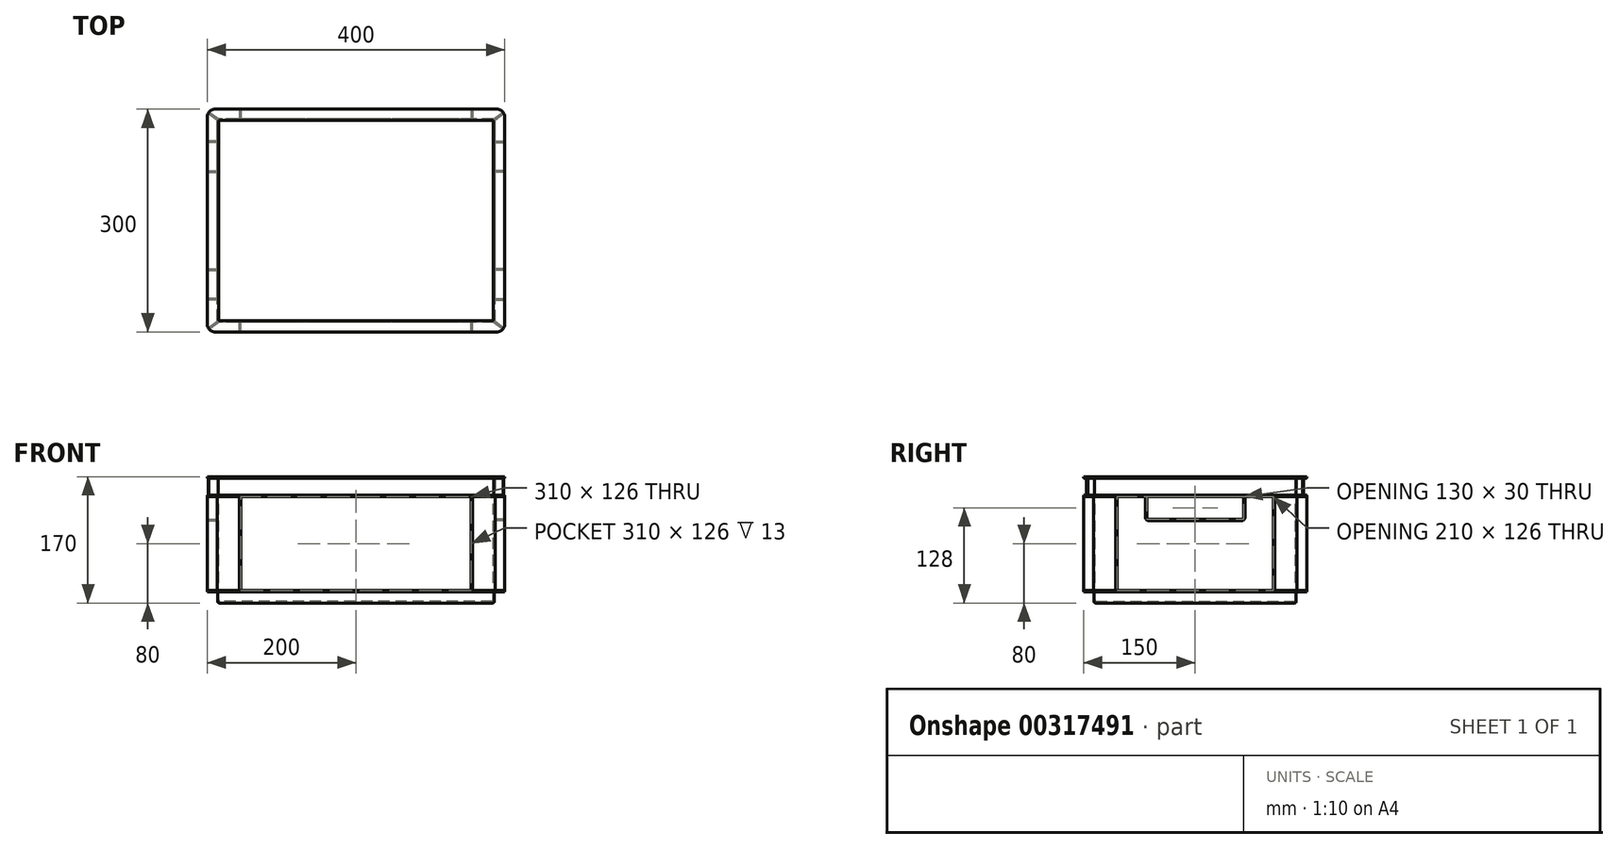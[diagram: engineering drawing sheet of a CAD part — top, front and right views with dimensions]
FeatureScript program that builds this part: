
annotation { "Feature Type Name" : "Feature", "Feature Type Description" : "" }
export const myFeature = defineFeature(function(context is Context, id is Id, definition is map)
    precondition{}
    {
        {
            var Q0;
            Q0=qCreatedBy(makeId("Top.planeOp"),FACE);
            var sketch = newSketch(context, id + "F0", { "sketchPlane" : qUnion([Q0])});
            skLineSegment(sketch, "E0.bottom", {"start": v(186, -136) * mm, "end": v(-186, -136) * mm});
            skLineSegment(sketch, "E0.top", {"start": v(186, 136) * mm, "end": v(-186, 136) * mm});
            skLineSegment(sketch, "E0.left", {"start": v(186, -136) * mm, "end": v(186, 136) * mm});
            skLineSegment(sketch, "E0.right", {"start": v(-186, -136) * mm, "end": v(-186, 136) * mm});
            skPoint(sketch, "E0.middle", {"position": v(0, 0) * mm});
            skPoint(sketch, "E1.visualSharp", {"position": v(-186, 136) * mm});
            skPoint(sketch, "E2.visualSharp", {"position": v(186, 136) * mm});
            skPoint(sketch, "E3.visualSharp", {"position": v(186, -136) * mm});
            skPoint(sketch, "E4.visualSharp", {"position": v(-186, -136) * mm});
            skSolve(sketch);
        }
        {
            var Q0;
            Q0=qSketchRegion(id+"F0",true);
            extrude(context, id + "F1", {"entities" : qUnion([Q0]), "depth" : 15 * mm});
        }
        {
            var Q0;
            Q0=makeQuery(id+"F1.opExtrude","CAP_FACE",FACE,{"disambiguationData":[OSD([sQuery(id+"F0.wireOp",EDGE,"E0.bottom"),sQuery(id+"F0.wireOp",EDGE,"E0.top"),sQuery(id+"F0.wireOp",EDGE,"E0.left"),sQuery(id+"F0.wireOp",EDGE,"E0.right")])],"isStart":false});
            var sketch = newSketch(context, id + "F2", { "sketchPlane" : qUnion([Q0])});
            skLineSegment(sketch, "E5.bottom", {"start": v(190, -150) * mm, "end": v(-190, -150) * mm});
            skLineSegment(sketch, "E5.top", {"start": v(190, 150) * mm, "end": v(-190, 150) * mm});
            skLineSegment(sketch, "E5.left", {"start": v(200, -140) * mm, "end": v(200, 140) * mm});
            skLineSegment(sketch, "E5.right", {"start": v(-200, -140) * mm, "end": v(-200, 140) * mm});
            skPoint(sketch, "E5.middle", {"position": v(0, 0) * mm});
            skPoint(sketch, "E6.visualSharp", {"position": v(-200, 150) * mm});
            skArc(sketch, "E6.filletArc", {"start": v(-190, 150) * mm, "mid": v(-197.07, 147.07) * mm, "end": v(-200, 140) * mm});
            skPoint(sketch, "E7.visualSharp", {"position": v(200, 150) * mm});
            skArc(sketch, "E7.filletArc", {"start": v(200, 140) * mm, "mid": v(197.07, 147.07) * mm, "end": v(190, 150) * mm});
            skPoint(sketch, "E8.visualSharp", {"position": v(200, -150) * mm});
            skArc(sketch, "E8.filletArc", {"start": v(190, -150) * mm, "mid": v(197.07, -147.07) * mm, "end": v(200, -140) * mm});
            skPoint(sketch, "E9.visualSharp", {"position": v(-200, -150) * mm});
            skArc(sketch, "E9.filletArc", {"start": v(-200, -140) * mm, "mid": v(-197.07, -147.07) * mm, "end": v(-190, -150) * mm});
            skSolve(sketch);
        }
        {
            var Q0;
            Q0=makeQuery(id+"F2.imprint","IMPRINT",FACE,{"disambiguationData":[TD([[makeQuery(id+"F2.imprint","IMPRINT",EDGE,{"derivedFrom":makeQuery(id+"F1.opExtrude","CAP_EDGE",EDGE,{"disambiguationData":[OSD([sQuery(id+"F0.wireOp",EDGE,"E0.bottom")])],"isStart":false})}),-1.0]])]});
            var Q1;
            Q1=makeQuery(id+"F2.imprint","IMPRINT",FACE,{"disambiguationData":[TD([[makeQuery(id+"F2.imprint","IMPRINT",EDGE,{"derivedFrom":sQuery(id+"F2.wireOp",EDGE,"E5.bottom")}),-1.0]])]});
            extrude(context, id + "F3", {"entities" : qUnion([Q0, Q1]), "operationType" : NewBodyOperationType.ADD, "depth" : 2 * mm});
        }
        {
            var Q0;
            Q0=makeQuery(id+"F3.opExtrude","CAP_FACE",FACE,{"disambiguationData":[OSD([sQuery(id+"F2.wireOp",EDGE,"E5.bottom"),sQuery(id+"F2.wireOp",EDGE,"E5.top"),sQuery(id+"F2.wireOp",EDGE,"E5.left"),sQuery(id+"F2.wireOp",EDGE,"E5.right"),sQuery(id+"F2.wireOp",EDGE,"E6.filletArc"),sQuery(id+"F2.wireOp",EDGE,"E7.filletArc"),sQuery(id+"F2.wireOp",EDGE,"E8.filletArc"),sQuery(id+"F2.wireOp",EDGE,"E9.filletArc")])],"isStart":false});
            var sketch = newSketch(context, id + "F4", { "sketchPlane" : qUnion([Q0])});
            skLineSegment(sketch, "E10.bottom", {"start": v(187, -137) * mm, "end": v(157, -137) * mm});
            skLineSegment(sketch, "E10.top", {"start": v(187, 137) * mm, "end": v(157, 137) * mm});
            skLineSegment(sketch, "E10.left", {"start": v(187, -137) * mm, "end": v(187, -107) * mm});
            skLineSegment(sketch, "E10.right", {"start": v(-187, -137) * mm, "end": v(-187, -107) * mm});
            skPoint(sketch, "E10.middle", {"position": v(0, 0) * mm});
            skLineSegment(sketch, "E11.bottom", {"start": v(-155, -150) * mm, "end": v(-157, -150) * mm});
            skLineSegment(sketch, "E11.left", {"start": v(-155, -150) * mm, "end": v(-155, -137) * mm});
            skLineSegment(sketch, "E11.right", {"start": v(-157, -150) * mm, "end": v(-157, -137) * mm});
            skPoint(sketch, "E11.middle", {"position": v(-156, -143.5) * mm});
            skLineSegment(sketch, "E12.trimOffspring", {"start": v(-157, -137) * mm, "end": v(-187, -137) * mm});
            skLineSegment(sketch, "E13.bottom", {"start": v(-187, -107) * mm, "end": v(-200, -107) * mm});
            skLineSegment(sketch, "E13.top", {"start": v(-187, -105) * mm, "end": v(-200, -105) * mm});
            skLineSegment(sketch, "E13.right", {"start": v(-200, -107) * mm, "end": v(-200, -105) * mm});
            skPoint(sketch, "E13.middle", {"position": v(-193.5, -106) * mm});
            skLineSegment(sketch, "E14.trimOffspring", {"start": v(-187, -105) * mm, "end": v(-187, 105) * mm});
            skLineSegment(sketch, "E15.MirrorCS", {"start": v(200, -107) * mm, "end": v(200, -105) * mm});
            skLineSegment(sketch, "E16.MirrorCS", {"start": v(155, -150) * mm, "end": v(155, -137) * mm});
            skLineSegment(sketch, "E17.MirrorCS", {"start": v(155, -150) * mm, "end": v(157, -150) * mm});
            skLineSegment(sketch, "E18.MirrorCS", {"start": v(157, -150) * mm, "end": v(157, -137) * mm});
            skLineSegment(sketch, "E19.MirrorCS", {"start": v(187, -105) * mm, "end": v(200, -105) * mm});
            skLineSegment(sketch, "E20.MirrorCS", {"start": v(187, -107) * mm, "end": v(200, -107) * mm});
            skPoint(sketch, "E21.MirrorP", {"position": v(193.5, -106) * mm});
            skLineSegment(sketch, "E22.trimOffspring", {"start": v(187, -105) * mm, "end": v(187, 105) * mm});
            skLineSegment(sketch, "E23.trimOffspring", {"start": v(155, -137) * mm, "end": v(-155, -137) * mm});
            skLineSegment(sketch, "E24.MirrorCS", {"start": v(-200, 107) * mm, "end": v(-200, 105) * mm});
            skPoint(sketch, "E25.MirrorP", {"position": v(-193.5, 106) * mm});
            skLineSegment(sketch, "E26.MirrorCS", {"start": v(-187, 105) * mm, "end": v(-200, 105) * mm});
            skLineSegment(sketch, "E27.MirrorCS", {"start": v(-187, 107) * mm, "end": v(-200, 107) * mm});
            skLineSegment(sketch, "E28.MirrorCS", {"start": v(-155, 150) * mm, "end": v(-157, 150) * mm});
            skLineSegment(sketch, "E29.MirrorCS", {"start": v(-157, 150) * mm, "end": v(-157, 137) * mm});
            skPoint(sketch, "E30.MirrorP", {"position": v(-156, 143.5) * mm});
            skLineSegment(sketch, "E31.MirrorCS", {"start": v(-155, 150) * mm, "end": v(-155, 137) * mm});
            skLineSegment(sketch, "E32.MirrorCS", {"start": v(155, 150) * mm, "end": v(157, 150) * mm});
            skLineSegment(sketch, "E33.MirrorCS", {"start": v(155, 150) * mm, "end": v(155, 137) * mm});
            skLineSegment(sketch, "E34.MirrorCS", {"start": v(157, 150) * mm, "end": v(157, 137) * mm});
            skLineSegment(sketch, "E35.MirrorCS", {"start": v(200, 107) * mm, "end": v(200, 105) * mm});
            skLineSegment(sketch, "E36.MirrorCS", {"start": v(187, 105) * mm, "end": v(200, 105) * mm});
            skPoint(sketch, "E37.MirrorP", {"position": v(193.5, 106) * mm});
            skLineSegment(sketch, "E38.MirrorCS", {"start": v(187, 107) * mm, "end": v(200, 107) * mm});
            skLineSegment(sketch, "E39.trimOffspring", {"start": v(-187, 107) * mm, "end": v(-187, 137) * mm});
            skLineSegment(sketch, "E40.trimOffspring", {"start": v(-157, 137) * mm, "end": v(-187, 137) * mm});
            skLineSegment(sketch, "E41.trimOffspring", {"start": v(155, 137) * mm, "end": v(-155, 137) * mm});
            skLineSegment(sketch, "E42.trimOffspring", {"start": v(187, 107) * mm, "end": v(187, 137) * mm});
            skSolve(sketch);
        }
        {
            var Q0;
            Q0=qSketchRegion(id+"F4",true);
            extrude(context, id + "F5", {"entities" : qUnion([Q0]), "operationType" : NewBodyOperationType.ADD, "depth" : 126 * mm});
        }
        {
            var Q0;
            Q0=makeQuery(id+"F5.opExtrude","CAP_FACE",FACE,{"disambiguationData":[OSD([sQuery(id+"F4.wireOp",EDGE,"E10.bottom"),sQuery(id+"F4.wireOp",EDGE,"E10.top"),sQuery(id+"F4.wireOp",EDGE,"E10.left"),sQuery(id+"F4.wireOp",EDGE,"E10.right")])],"isStart":false});
            var sketch = newSketch(context, id + "F6", { "sketchPlane" : qUnion([Q0])});
            skArc(sketch, "E43.0", {"start": v(-190, 150) * mm, "mid": v(-197.07, 147.07) * mm, "end": v(-200, 140) * mm});
            skArc(sketch, "E43.1", {"start": v(-200, -140) * mm, "mid": v(-197.07, -147.07) * mm, "end": v(-190, -150) * mm});
            skArc(sketch, "E43.2", {"start": v(190, -150) * mm, "mid": v(197.07, -147.07) * mm, "end": v(200, -140) * mm});
            skArc(sketch, "E43.3", {"start": v(200, 140) * mm, "mid": v(197.07, 147.07) * mm, "end": v(190, 150) * mm});
            skLineSegment(sketch, "E44", {"start": v(-200, 140) * mm, "end": v(-200, -140) * mm});
            skLineSegment(sketch, "E45", {"start": v(-190, -150) * mm, "end": v(190, -150) * mm});
            skLineSegment(sketch, "E46", {"start": v(200, 140) * mm, "end": v(200, -140) * mm});
            skLineSegment(sketch, "E47", {"start": v(-190, 150) * mm, "end": v(190, 150) * mm});
            skSolve(sketch);
        }
        {
            var Q0;
            Q0=qSketchRegion(id+"F6",true);
            extrude(context, id + "F7", {"entities" : qUnion([Q0]), "operationType" : NewBodyOperationType.ADD, "depth" : 2 * mm});
        }
        {
            var Q0;
            Q0=makeQuery(id+"F7.opExtrude","CAP_FACE",FACE,{"disambiguationData":[OSD([sQuery(id+"F6.wireOp",EDGE,"E43.0"),sQuery(id+"F6.wireOp",EDGE,"E43.1"),sQuery(id+"F6.wireOp",EDGE,"E43.2"),sQuery(id+"F6.wireOp",EDGE,"E43.3"),sQuery(id+"F6.wireOp",EDGE,"E44"),sQuery(id+"F6.wireOp",EDGE,"E45"),sQuery(id+"F6.wireOp",EDGE,"E46"),sQuery(id+"F6.wireOp",EDGE,"E47")])],"isStart":false});
            var sketch = newSketch(context, id + "F8", { "sketchPlane" : qUnion([Q0])});
            skLineSegment(sketch, "E48.bottom", {"start": v(185.3, -137) * mm, "end": v(-185.3, -137) * mm});
            skLineSegment(sketch, "E48.top", {"start": v(185.3, 137) * mm, "end": v(-185.3, 137) * mm});
            skLineSegment(sketch, "E48.left", {"start": v(187, -135.76) * mm, "end": v(187, 135.76) * mm});
            skLineSegment(sketch, "E48.right", {"start": v(-187, -135.76) * mm, "end": v(-187, 135.76) * mm});
            skPoint(sketch, "E48.middle", {"position": v(0, 0) * mm});
            skLineSegment(sketch, "E49", {"start": v(-187, 137) * mm, "end": v(187, -137) * mm, "construction": true});
            skLineSegment(sketch, "E50.0", {"start": v(-198.93, 144.5) * mm, "end": v(-187, 135.76) * mm});
            skLineSegment(sketch, "E51.0", {"start": v(-197.85, 146.2) * mm, "end": v(-185.3, 137) * mm});
            skArc(sketch, "E52.0", {"start": v(-197.85, 146.2) * mm, "mid": v(-198.43, 145.37) * mm, "end": v(-198.93, 144.5) * mm});
            skPoint(sketch, "E53.orphan", {"position": v(-190, 150) * mm});
            skPoint(sketch, "E54.orphan", {"position": v(-200, 140) * mm});
            skArc(sketch, "E55.0", {"start": v(197.85, -146.2) * mm, "mid": v(198.43, -145.37) * mm, "end": v(198.93, -144.5) * mm});
            skPoint(sketch, "E56.orphan", {"position": v(200, -140) * mm});
            skPoint(sketch, "E57.orphan", {"position": v(190, -150) * mm});
            skLineSegment(sketch, "E58.trimOffspring", {"start": v(187, -135.76) * mm, "end": v(198.93, -144.5) * mm});
            skLineSegment(sketch, "E59.trimOffspring", {"start": v(185.3, -137) * mm, "end": v(197.85, -146.2) * mm});
            skLineSegment(sketch, "E60.MirrorCS", {"start": v(-197.85, -146.2) * mm, "end": v(-185.3, -137) * mm});
            skPoint(sketch, "E61.MirrorP", {"position": v(-200, -140) * mm});
            skArc(sketch, "E62.MirrorCS", {"start": v(-197.85, -146.2) * mm, "mid": v(-198.43, -145.37) * mm, "end": v(-198.93, -144.5) * mm});
            skLineSegment(sketch, "E63.MirrorCS", {"start": v(-198.93, -144.5) * mm, "end": v(-187, -135.76) * mm});
            skPoint(sketch, "E64.MirrorP", {"position": v(-190, -150) * mm});
            skArc(sketch, "E65.MirrorCS", {"start": v(197.85, 146.2) * mm, "mid": v(198.43, 145.37) * mm, "end": v(198.93, 144.5) * mm});
            skPoint(sketch, "E66.MirrorP", {"position": v(200, 140) * mm});
            skPoint(sketch, "E67.MirrorP", {"position": v(190, 150) * mm});
            skLineSegment(sketch, "E68.MirrorCS", {"start": v(187, 135.76) * mm, "end": v(198.93, 144.5) * mm});
            skLineSegment(sketch, "E69.MirrorCS", {"start": v(185.3, 137) * mm, "end": v(197.85, 146.2) * mm});
            skPoint(sketch, "E70.orphan", {"position": v(187, 137) * mm});
            skPoint(sketch, "E71.orphan", {"position": v(-187, -137) * mm});
            skSolve(sketch);
        }
        {
            var Q0;
            Q0=qSketchRegion(id+"F8",true);
            extrude(context, id + "F9", {"entities" : qUnion([Q0]), "operationType" : NewBodyOperationType.ADD, "depth" : 23 * mm});
        }
        {
            var Q0;
            Q0=makeQuery(id+"F9.opExtrude","CAP_FACE",FACE,{"disambiguationData":[OSD([sQuery(id+"F8.wireOp",EDGE,"E48.bottom"),sQuery(id+"F8.wireOp",EDGE,"E48.top"),sQuery(id+"F8.wireOp",EDGE,"E48.left"),sQuery(id+"F8.wireOp",EDGE,"E48.right"),sQuery(id+"F8.wireOp",EDGE,"E50.0"),sQuery(id+"F8.wireOp",EDGE,"E51.0"),sQuery(id+"F8.wireOp",EDGE,"E52.0"),sQuery(id+"F8.wireOp",EDGE,"E55.0"),sQuery(id+"F8.wireOp",EDGE,"E58.trimOffspring"),sQuery(id+"F8.wireOp",EDGE,"E59.trimOffspring"),sQuery(id+"F8.wireOp",EDGE,"E60.MirrorCS"),sQuery(id+"F8.wireOp",EDGE,"E62.MirrorCS"),sQuery(id+"F8.wireOp",EDGE,"E63.MirrorCS"),sQuery(id+"F8.wireOp",EDGE,"E65.MirrorCS"),sQuery(id+"F8.wireOp",EDGE,"E68.MirrorCS"),sQuery(id+"F8.wireOp",EDGE,"E69.MirrorCS")])],"isStart":false});
            var sketch = newSketch(context, id + "F10", { "sketchPlane" : qUnion([Q0])});
            skArc(sketch, "E72.0", {"start": v(190, -150) * mm, "mid": v(197.07, -147.07) * mm, "end": v(200, -140) * mm});
            skArc(sketch, "E73.0", {"start": v(-200, -140) * mm, "mid": v(-197.07, -147.07) * mm, "end": v(-190, -150) * mm});
            skArc(sketch, "E74.0", {"start": v(200, 140) * mm, "mid": v(197.07, 147.07) * mm, "end": v(190, 150) * mm});
            skLineSegment(sketch, "E75.0", {"start": v(200, -140) * mm, "end": v(200, 140) * mm});
            skLineSegment(sketch, "E76.0", {"start": v(190, 150) * mm, "end": v(-190, 150) * mm});
            skLineSegment(sketch, "E77.0", {"start": v(190, -150) * mm, "end": v(-190, -150) * mm});
            skLineSegment(sketch, "E78.0", {"start": v(-200, -140) * mm, "end": v(-200, 140) * mm});
            skArc(sketch, "E79.0", {"start": v(-190, 150) * mm, "mid": v(-197.07, 147.07) * mm, "end": v(-200, 140) * mm});
            skSolve(sketch);
        }
        {
            var Q0;
            Q0=qSketchRegion(id+"F10",true);
            extrude(context, id + "F11", {"entities" : qUnion([Q0]), "operationType" : NewBodyOperationType.ADD, "depth" : 2 * mm});
        }
        {
            var Q0;
            Q0=makeQuery(id+"F11.opExtrude","CAP_FACE",FACE,{"disambiguationData":[OSD([sQuery(id+"F10.wireOp",EDGE,"E72.0"),sQuery(id+"F10.wireOp",EDGE,"E73.0"),sQuery(id+"F10.wireOp",EDGE,"E74.0"),sQuery(id+"F10.wireOp",EDGE,"E75.0"),sQuery(id+"F10.wireOp",EDGE,"E76.0"),sQuery(id+"F10.wireOp",EDGE,"E77.0"),sQuery(id+"F10.wireOp",EDGE,"E78.0"),sQuery(id+"F10.wireOp",EDGE,"E79.0")])],"isStart":false});
            var sketch = newSketch(context, id + "F12", { "sketchPlane" : qUnion([Q0])});
            skLineSegment(sketch, "E80.bottom", {"start": v(185, -135) * mm, "end": v(-185, -135) * mm});
            skLineSegment(sketch, "E80.top", {"start": v(185, 135) * mm, "end": v(-185, 135) * mm});
            skLineSegment(sketch, "E80.left", {"start": v(185, -135) * mm, "end": v(185, 135) * mm});
            skLineSegment(sketch, "E80.right", {"start": v(-185, -135) * mm, "end": v(-185, 135) * mm});
            skPoint(sketch, "E80.middle", {"position": v(0, 0) * mm});
            skSolve(sketch);
        }
        {
            var Q0;
            Q0=qSketchRegion(id+"F12",true);
            extrude(context, id + "F13", {"entities" : qUnion([Q0]), "operationType" : NewBodyOperationType.REMOVE, "oppositeDirection" : true, "depth" : 168 * mm});
        }
        {
            var Q0;
            Q0=makeQuery(id+"F5.opExtrude","SWEPT_FACE",FACE,{"disambiguationData":[OSD([sQuery(id+"F4.wireOp",EDGE,"E14.trimOffspring")])]});
            var sketch = newSketch(context, id + "F14", { "sketchPlane" : qUnion([Q0])});
            skLineSegment(sketch, "E81.bottom", {"start": v(63, 111) * mm, "end": v(-63, 111) * mm});
            skLineSegment(sketch, "E81.left", {"start": v(67, 115) * mm, "end": v(67, 143) * mm});
            skLineSegment(sketch, "E81.right", {"start": v(-67, 115) * mm, "end": v(-67, 143) * mm});
            skPoint(sketch, "E81.middle", {"position": v(0, 109.39) * mm});
            skLineSegment(sketch, "E82.bottom", {"start": v(63, 113) * mm, "end": v(-63, 113) * mm});
            skLineSegment(sketch, "E82.left", {"start": v(65, 115) * mm, "end": v(65, 143) * mm});
            skLineSegment(sketch, "E82.right", {"start": v(-65, 115) * mm, "end": v(-65, 143) * mm});
            skLineSegment(sketch, "E83.0", {"start": v(-67, 143) * mm, "end": v(-65, 143) * mm});
            skPoint(sketch, "E84.orphan", {"position": v(-67, 107.78) * mm});
            skPoint(sketch, "E85.orphan", {"position": v(-65, 105.78) * mm});
            skPoint(sketch, "E86.orphan", {"position": v(65, 105.78) * mm});
            skPoint(sketch, "E87.orphan", {"position": v(67, 107.78) * mm});
            skLineSegment(sketch, "E88.trimOffspring", {"start": v(65, 143) * mm, "end": v(67, 143) * mm});
            skPoint(sketch, "E89.orphan", {"position": v(-105, 143) * mm});
            skPoint(sketch, "E90.orphan", {"position": v(105, 143) * mm});
            skPoint(sketch, "E91.visualSharp", {"position": v(-67, 111) * mm});
            skArc(sketch, "E91.filletArc", {"start": v(-67, 115) * mm, "mid": v(-65.83, 112.17) * mm, "end": v(-63, 111) * mm});
            skPoint(sketch, "E92.visualSharp", {"position": v(67, 111) * mm});
            skArc(sketch, "E92.filletArc", {"start": v(63, 111) * mm, "mid": v(65.83, 112.17) * mm, "end": v(67, 115) * mm});
            skPoint(sketch, "E93.visualSharp", {"position": v(65, 113) * mm});
            skArc(sketch, "E93.filletArc", {"start": v(63, 113) * mm, "mid": v(64.41, 113.59) * mm, "end": v(65, 115) * mm});
            skPoint(sketch, "E94.visualSharp", {"position": v(-65, 113) * mm});
            skArc(sketch, "E94.filletArc", {"start": v(-65, 115) * mm, "mid": v(-64.41, 113.59) * mm, "end": v(-63, 113) * mm});
            skSolve(sketch);
        }
        {
            var Q0;
            Q0=qSketchRegion(id+"F14",true);
            var Q1;
            Q1=makeQuery(id+"F7.boolean.opBoolean","MERGE",FACE,{"derivedFrom":[makeQuery(id+"F5.boolean.opBoolean","MERGE",FACE,{"derivedFrom":[makeQuery(id+"F3.opExtrude","SWEPT_FACE",FACE,{"disambiguationData":[OSD([sQuery(id+"F2.wireOp",EDGE,"E5.right")])]}),makeQuery(id+"F5.opExtrude","SWEPT_FACE",FACE,{"disambiguationData":[OSD([sQuery(id+"F4.wireOp",EDGE,"E13.right")])]}),makeQuery(id+"F5.opExtrude","SWEPT_FACE",FACE,{"disambiguationData":[OSD([sQuery(id+"F4.wireOp",EDGE,"E24.MirrorCS")])]})]}),makeQuery(id+"F7.opExtrude","SWEPT_FACE",FACE,{"disambiguationData":[OSD([sQuery(id+"F6.wireOp",EDGE,"E44")])]})]});
            extrude(context, id + "F15", {"entities" : qUnion([Q0]), "operationType" : NewBodyOperationType.ADD, "endBound" : BoundingType.UP_TO_SURFACE, "endBoundEntityFace" : qUnion([Q1]), "depth" : 25 * mm});
        }
        {
            var Q0;
            Q0=makeQuery(id+"F5.opExtrude","SWEPT_FACE",FACE,{"disambiguationData":[OSD([sQuery(id+"F4.wireOp",EDGE,"E22.trimOffspring")])]});
            var sketch = newSketch(context, id + "F16", { "sketchPlane" : qUnion([Q0])});
            skLineSegment(sketch, "E95.0", {"start": v(67, 115) * mm, "end": v(67, 143) * mm});
            skArc(sketch, "E95.1", {"start": v(67, 115) * mm, "mid": v(65.83, 112.17) * mm, "end": v(63, 111) * mm});
            skLineSegment(sketch, "E95.2", {"start": v(-63, 111) * mm, "end": v(63, 111) * mm});
            skLineSegment(sketch, "E95.3", {"start": v(-63, 113) * mm, "end": v(63, 113) * mm});
            skLineSegment(sketch, "E95.4", {"start": v(65, 115) * mm, "end": v(65, 143) * mm});
            skArc(sketch, "E95.5", {"start": v(65, 115) * mm, "mid": v(64.41, 113.59) * mm, "end": v(63, 113) * mm});
            skArc(sketch, "E95.6", {"start": v(-63, 113) * mm, "mid": v(-64.41, 113.59) * mm, "end": v(-65, 115) * mm});
            skArc(sketch, "E95.7", {"start": v(-63, 111) * mm, "mid": v(-65.83, 112.17) * mm, "end": v(-67, 115) * mm});
            skLineSegment(sketch, "E95.8", {"start": v(-67, 115) * mm, "end": v(-67, 143) * mm});
            skLineSegment(sketch, "E95.9", {"start": v(-65, 115) * mm, "end": v(-65, 143) * mm});
            skLineSegment(sketch, "E96", {"start": v(67, 143) * mm, "end": v(65, 143) * mm});
            skLineSegment(sketch, "E97", {"start": v(-65, 143) * mm, "end": v(-67, 143) * mm});
            skSolve(sketch);
        }
        {
            var Q0;
            Q0=qSketchRegion(id+"F16",true);
            var Q1;
            Q1=makeQuery(id+"F7.boolean.opBoolean","MERGE",FACE,{"derivedFrom":[makeQuery(id+"F5.boolean.opBoolean","MERGE",FACE,{"derivedFrom":[makeQuery(id+"F3.opExtrude","SWEPT_FACE",FACE,{"disambiguationData":[OSD([sQuery(id+"F2.wireOp",EDGE,"E5.left")])]}),makeQuery(id+"F5.opExtrude","SWEPT_FACE",FACE,{"disambiguationData":[OSD([sQuery(id+"F4.wireOp",EDGE,"E15.MirrorCS")])]}),makeQuery(id+"F5.opExtrude","SWEPT_FACE",FACE,{"disambiguationData":[OSD([sQuery(id+"F4.wireOp",EDGE,"E35.MirrorCS")])]})]}),makeQuery(id+"F7.opExtrude","SWEPT_FACE",FACE,{"disambiguationData":[OSD([sQuery(id+"F6.wireOp",EDGE,"E46")])]})]});
            extrude(context, id + "F17", {"entities" : qUnion([Q0]), "operationType" : NewBodyOperationType.ADD, "endBound" : BoundingType.UP_TO_SURFACE, "endBoundEntityFace" : qUnion([Q1]), "depth" : 25 * mm});
        }
        {
            var Q0;
            Q0=makeQuery(id+"F13.boolean.opBoolean","COPY",EDGE,{"derivedFrom":makeQuery(id+"F13.opExtrude","SWEPT_EDGE",EDGE,{"disambiguationData":[OSD([sQuery(id+"F12.wireOp",EDGE,"E80.bottom"),sQuery(id+"F12.wireOp",EDGE,"E80.right")])]})});
            var Q1;
            Q1=makeQuery(id+"F13.boolean.opBoolean","COPY",EDGE,{"derivedFrom":makeQuery(id+"F13.opExtrude","SWEPT_EDGE",EDGE,{"disambiguationData":[OSD([sQuery(id+"F12.wireOp",EDGE,"E80.bottom"),sQuery(id+"F12.wireOp",EDGE,"E80.left")])]})});
            var Q2;
            Q2=makeQuery(id+"F13.boolean.opBoolean","COPY",EDGE,{"derivedFrom":makeQuery(id+"F13.opExtrude","SWEPT_EDGE",EDGE,{"disambiguationData":[OSD([sQuery(id+"F12.wireOp",EDGE,"E80.top"),sQuery(id+"F12.wireOp",EDGE,"E80.left")])]})});
            var Q3;
            Q3=makeQuery(id+"F13.boolean.opBoolean","COPY",EDGE,{"derivedFrom":makeQuery(id+"F13.opExtrude","CAP_EDGE",EDGE,{"disambiguationData":[OSD([sQuery(id+"F12.wireOp",EDGE,"E80.top")])],"isStart":false})});
            var Q4;
            Q4=makeQuery(id+"F13.boolean.opBoolean","COPY",EDGE,{"derivedFrom":makeQuery(id+"F13.opExtrude","CAP_EDGE",EDGE,{"disambiguationData":[OSD([sQuery(id+"F12.wireOp",EDGE,"E80.left")])],"isStart":false})});
            var Q5;
            Q5=makeQuery(id+"F13.boolean.opBoolean","COPY",EDGE,{"derivedFrom":makeQuery(id+"F13.opExtrude","CAP_EDGE",EDGE,{"disambiguationData":[OSD([sQuery(id+"F12.wireOp",EDGE,"E80.bottom")])],"isStart":false})});
            var Q6;
            Q6=makeQuery(id+"F13.boolean.opBoolean","COPY",EDGE,{"derivedFrom":makeQuery(id+"F13.opExtrude","CAP_EDGE",EDGE,{"disambiguationData":[OSD([sQuery(id+"F12.wireOp",EDGE,"E80.right")])],"isStart":false})});
            var Q7;
            Q7=makeQuery(id+"F13.boolean.opBoolean","COPY",EDGE,{"derivedFrom":makeQuery(id+"F13.opExtrude","SWEPT_EDGE",EDGE,{"disambiguationData":[OSD([sQuery(id+"F12.wireOp",EDGE,"E80.top"),sQuery(id+"F12.wireOp",EDGE,"E80.right")])]})});
            var Q8;
            Q8=makeQuery(id+"F5.opExtrude","SWEPT_EDGE",EDGE,{"disambiguationData":[OSD([sQuery(id+"F4.wireOp",EDGE,"E10.bottom"),sQuery(id+"F4.wireOp",EDGE,"E10.left")])]});
            var Q9;
            Q9=makeQuery(id+"F5.opExtrude","SWEPT_EDGE",EDGE,{"disambiguationData":[OSD([sQuery(id+"F4.wireOp",EDGE,"E10.top"),sQuery(id+"F4.wireOp",EDGE,"E42.trimOffspring")])]});
            var Q10;
            Q10=makeQuery(id+"F5.opExtrude","SWEPT_EDGE",EDGE,{"disambiguationData":[OSD([sQuery(id+"F4.wireOp",EDGE,"E39.trimOffspring"),sQuery(id+"F4.wireOp",EDGE,"E40.trimOffspring")])]});
            var Q11;
            Q11=makeQuery(id+"F5.opExtrude","SWEPT_EDGE",EDGE,{"disambiguationData":[OSD([sQuery(id+"F4.wireOp",EDGE,"E10.right"),sQuery(id+"F4.wireOp",EDGE,"E12.trimOffspring")])]});
            var Q12;
            Q12=makeQuery(id+"F1.opExtrude","CAP_EDGE",EDGE,{"disambiguationData":[OSD([sQuery(id+"F0.wireOp",EDGE,"E0.left")])],"isStart":true});
            var Q13;
            Q13=makeQuery(id+"F1.opExtrude","CAP_EDGE",EDGE,{"disambiguationData":[OSD([sQuery(id+"F0.wireOp",EDGE,"E0.top")])],"isStart":true});
            var Q14;
            Q14=makeQuery(id+"F1.opExtrude","SWEPT_EDGE",EDGE,{"disambiguationData":[OSD([sQuery(id+"F0.wireOp",EDGE,"E0.top"),sQuery(id+"F0.wireOp",EDGE,"E0.left")])]});
            var Q15;
            Q15=makeQuery(id+"F1.opExtrude","CAP_EDGE",EDGE,{"disambiguationData":[OSD([sQuery(id+"F0.wireOp",EDGE,"E0.bottom")])],"isStart":true});
            var Q16;
            Q16=makeQuery(id+"F1.opExtrude","SWEPT_EDGE",EDGE,{"disambiguationData":[OSD([sQuery(id+"F0.wireOp",EDGE,"E0.bottom"),sQuery(id+"F0.wireOp",EDGE,"E0.left")])]});
            var Q17;
            Q17=makeQuery(id+"F1.opExtrude","SWEPT_EDGE",EDGE,{"disambiguationData":[OSD([sQuery(id+"F0.wireOp",EDGE,"E0.bottom"),sQuery(id+"F0.wireOp",EDGE,"E0.right")])]});
            var Q18;
            Q18=makeQuery(id+"F1.opExtrude","CAP_EDGE",EDGE,{"disambiguationData":[OSD([sQuery(id+"F0.wireOp",EDGE,"E0.right")])],"isStart":true});
            var Q19;
            Q19=makeQuery(id+"F1.opExtrude","SWEPT_EDGE",EDGE,{"disambiguationData":[OSD([sQuery(id+"F0.wireOp",EDGE,"E0.top"),sQuery(id+"F0.wireOp",EDGE,"E0.right")])]});
            fillet(context, id + "F18", {"entities" : qUnion([Q0, Q1, Q2, Q3, Q4, Q5, Q6, Q7, Q8, Q9, Q10, Q11, Q12, Q13, Q14, Q15, Q16, Q17, Q18, Q19]), "radius" : 2 * mm, "tangentPropagation" : true, "allowEdgeOverflow" : false});
        }
    });
